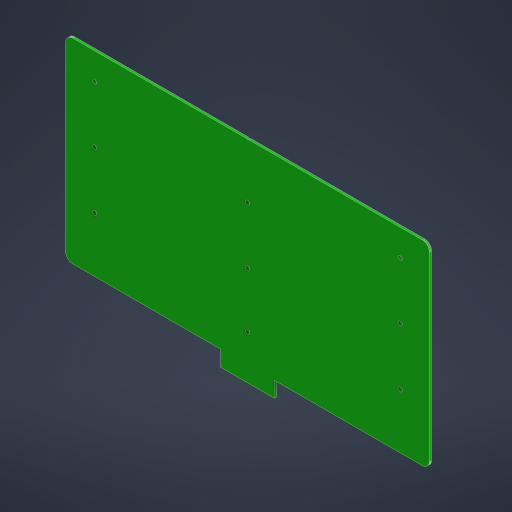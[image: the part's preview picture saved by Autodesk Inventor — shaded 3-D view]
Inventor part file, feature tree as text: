
AUTODESK INVENTOR PART (.ipt)
format: ipt  version: 2024.3 (Build 283343010, 343A)  size: 476,160 bytes
history: native  units: mm
features: extrude x3, sketch x1, chamfer x1
ambient origin geometry x8: Origin, YZ Plane, XZ Plane, XY Plane, X Axis, Y Axis, Z Axis, Center Point
bodies: Body1 (feature_tree)
feature tree (5):
  sketch  "Skizze1"  dims[d0=1.6mm d1=0.0mm d2=10.4mm d3=0.0mm d4=8.0mm d5=0.0mm d6=1.2mm d7=2.0mm d8=45.0deg]
  extrude  "Extrusion1"  Depth=10.4mm TaperAngle=0.0deg
  extrude  "Extrusion2"  Depth=8.0mm TaperAngle=0.0deg
  extrude  "Extrusion3"  Depth=1.2mm TaperAngle=45.0deg
  chamfer  "Fasen1"  [1 undecoded]
note: 1 required parameter value undecoded (feature->parameter linkage not recoverable at this tier; creation-order binding heuristic only, values carry confidence <= 0.55)
